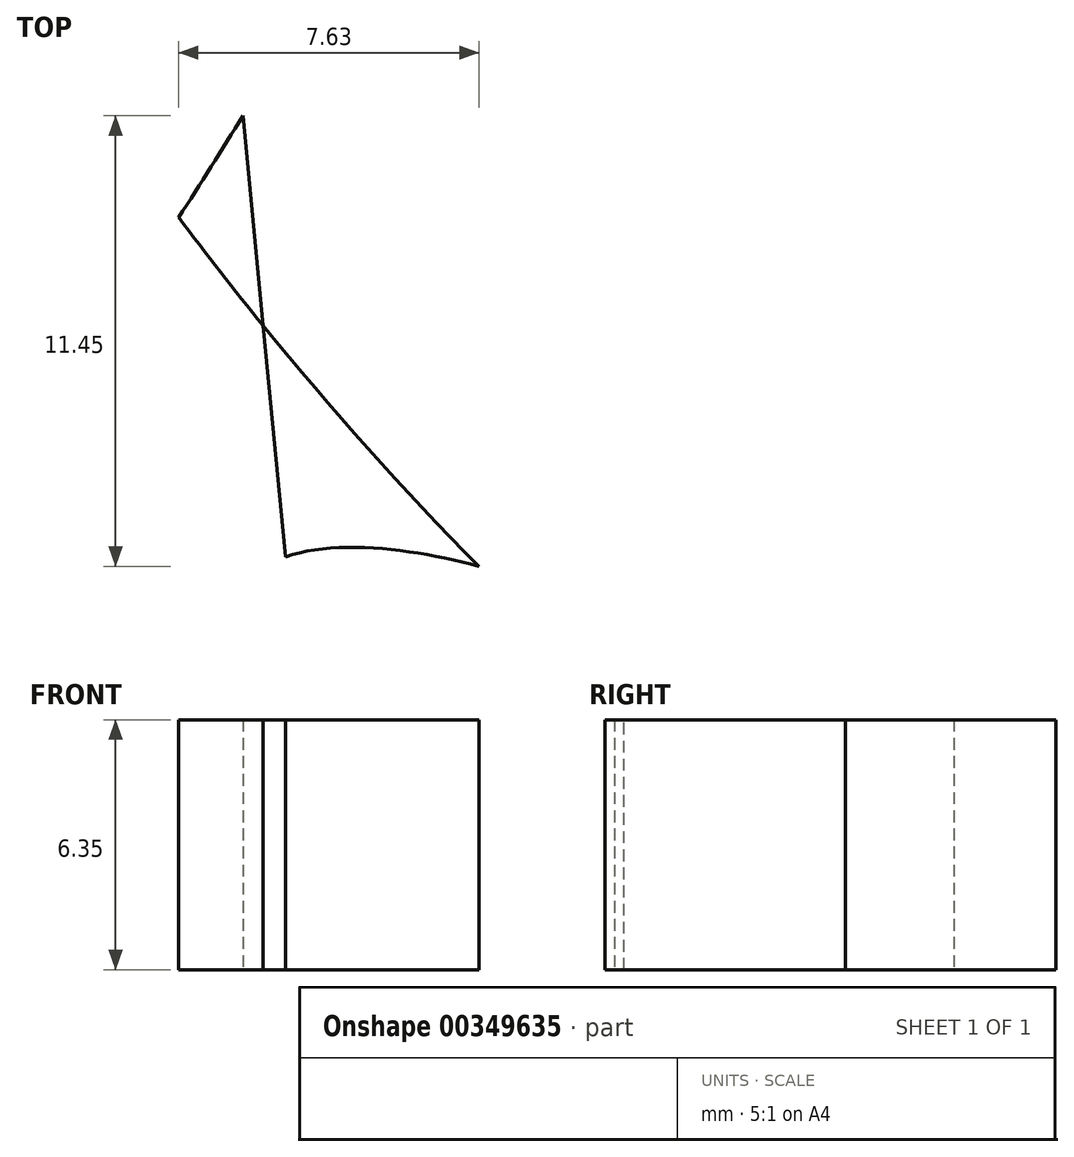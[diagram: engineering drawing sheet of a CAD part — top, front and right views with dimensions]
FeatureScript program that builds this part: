
annotation { "Feature Type Name" : "Feature", "Feature Type Description" : "" }
export const myFeature = defineFeature(function(context is Context, id is Id, definition is map)
    precondition{}
    {
        {
            var Q0;
            Q0=qCreatedBy(makeId("Top.planeOp"),FACE);
            var sketch = newSketch(context, id + "F0", { "sketchPlane" : qUnion([Q0])});
            skFitSpline(sketch, "E0", {"points": [v(-89.2, -72.37) * mm, v(-80.96, -69.32) * mm, v(-70.58, -66.57) * mm, v(-58.06, -63.52) * mm, v(-42.18, -61.08) * mm, v(-30.58, -59.24) * mm, v(-14.4, -58.33) * mm, v(2.7, -58.02) * mm, v(24.38, -58.02) * mm, v(45.14, -58.02) * mm, v(71.09, -58.02) * mm, v(96.43, -58.02) * mm, v(117.7, -59.07) * mm, v(146.1, -60.85) * mm, v(171.42, -62.58) * mm, v(182.87, -63.62) * mm, v(192.92, -64.66) * mm, v(205.06, -67.78) * mm, v(216.16, -72.64) * mm, v(220.67, -74.37) * mm, v(223.44, -78.54) * mm, v(225.87, -86.51) * mm, v(223.1, -93.8) * mm, v(217.2, -101.77) * mm, v(210.26, -105.24) * mm, v(204.02, -105.59) * mm, v(197.78, -102.81) * mm, v(185.99, -97.26) * mm, v(172.11, -92.4) * mm, v(159.28, -89.63) * mm, v(141.94, -86.51) * mm, v(125.64, -85.82) * mm, v(113.85, -86.17) * mm, v(104.49, -86.51) * mm, v(97.2, -88.94) * mm, v(93.04, -92.4) * mm, v(90.61, -95.88) * mm, v(89.23, -99) * mm, v(87.84, -100.73) * mm, v(85.41, -99.34) * mm, v(83.92, -93.7) * mm, v(81.94, -88.7) * mm, v(78.82, -86.86) * mm, v(73.53, -86.51) * mm, v(71.54, -88.6) * mm, v(70.85, -90.67) * mm, v(69.11, -92.06) * mm, v(62.87, -91.02) * mm, v(58.01, -89.98) * mm, v(49, -89.98) * mm, v(36.86, -91.02) * mm, v(24.72, -93.1) * mm, v(16.4, -94.84) * mm, v(6, -96.57) * mm, v(-5.1, -99.34) * mm, v(-19.67, -100.73) * mm, v(-29.38, -101.08) * mm, v(-37.36, -100.73) * mm, v(-44.3, -100.04) * mm, v(-54.7, -97.96) * mm, v(-61.98, -95.18) * mm, v(-71, -89.98) * mm, v(-75.86, -85.82) * mm, v(-89.2, -72.37) * mm]});
            skPoint(sketch, "E1.1.internal.orphan", {"position": v(73.53, -78.42) * mm});
            skPoint(sketch, "E2.1.internal.orphan", {"position": v(72.1, -82.53) * mm});
            skPoint(sketch, "E3.1.internal.orphan", {"position": v(73.53, -82.53) * mm});
            skLineSegment(sketch, "E4", {"start": v(73.53, -86.51) * mm, "end": v(71.83, -68.93) * mm});
            skLineSegment(sketch, "E5", {"start": v(68.17, -65.48) * mm, "end": v(-44.06, -61.37) * mm});
            skPoint(sketch, "E6.visualSharp", {"position": v(71.5, -65.6) * mm});
            skArc(sketch, "E6.filletArc", {"start": v(71.83, -68.93) * mm, "mid": v(70.65, -66.52) * mm, "end": v(68.17, -65.48) * mm});
            skCircle(sketch, "E7", {"center": v(209.21, -94.51) * mm, "radius": 4.76 * mm});
            skPoint(sketch, "E7.first.point", {"position": v(209.05, -99.27) * mm});
            skPoint(sketch, "E7.second.point", {"position": v(209.18, -89.75) * mm});
            skPoint(sketch, "E7.third.point", {"position": v(213.88, -93.56) * mm});
            skCircle(sketch, "E8", {"center": v(191.7, -78.8) * mm, "radius": 3.18 * mm});
            skPoint(sketch, "E8.first.point", {"position": v(191.75, -81.97) * mm});
            skPoint(sketch, "E8.second.point", {"position": v(191.63, -75.62) * mm});
            skPoint(sketch, "E8.third.point", {"position": v(194.8, -78.19) * mm});
            skCircle(sketch, "E9", {"center": v(123.5, -71.58) * mm, "radius": 3.18 * mm});
            skPoint(sketch, "E9.first.point", {"position": v(120.34, -71.87) * mm});
            skPoint(sketch, "E9.second.point", {"position": v(126.65, -71.2) * mm});
            skPoint(sketch, "E9.third.point", {"position": v(124.1, -74.7) * mm});
            skLineSegment(sketch, "E10", {"start": v(142.3, -60.6) * mm, "end": v(154.42, -61.38) * mm});
            skPoint(sketch, "E11.start.orphan", {"position": v(154.42, -70.9) * mm});
            skArc(sketch, "E12", {"start": v(172.79, -52.87) * mm, "mid": v(160.07, -46.61) * mm, "end": v(146.76, -51.46) * mm});
            skArc(sketch, "E13", {"start": v(220.67, -74.37) * mm, "mid": v(193.32, -64.98) * mm, "end": v(164.55, -62.06) * mm});
            skArc(sketch, "E14", {"start": v(220.67, -74.37) * mm, "mid": v(220.11, -81.8) * mm, "end": v(225.87, -86.51) * mm});
            skArc(sketch, "E15", {"start": v(8.92, 3.57) * mm, "mid": v(-27.84, 5.96) * mm, "end": v(-64.6, 8.29) * mm});
            skArc(sketch, "E16", {"start": v(54.16, -6.04) * mm, "mid": v(32.02, 1.01) * mm, "end": v(8.92, 3.57) * mm});
            skArc(sketch, "E17", {"start": v(225.22, -17.28) * mm, "mid": v(145.31, 73.87) * mm, "end": v(54.16, -6.04) * mm});
            skArc(sketch, "E18", {"start": v(54.16, -35.45) * mm, "mid": v(148.77, -111.9) * mm, "end": v(225.22, -17.28) * mm});
            skArc(sketch, "E19", {"start": v(202.98, -36.51) * mm, "mid": v(129.1, 38.43) * mm, "end": v(54.16, -35.45) * mm});
            skArc(sketch, "E20", {"start": v(202.98, -36.51) * mm, "mid": v(191.08, -30.63) * mm, "end": v(178.66, -25.96) * mm});
            skArc(sketch, "E21", {"start": v(178.66, -25.96) * mm, "mid": v(162.48, -21.52) * mm, "end": v(145.86, -19.17) * mm});
            skArc(sketch, "E22", {"start": v(145.86, -19.17) * mm, "mid": v(128.87, -16.97) * mm, "end": v(111.74, -17.28) * mm});
            skArc(sketch, "E23", {"start": v(111.74, -17.28) * mm, "mid": v(105.33, -17.9) * mm, "end": v(99.11, -19.55) * mm});
            skArc(sketch, "E24", {"start": v(99.11, -19.55) * mm, "mid": v(92.44, -23.97) * mm, "end": v(88.37, -30.86) * mm});
            skArc(sketch, "E25", {"start": v(84.03, -27.28) * mm, "mid": v(85.3, -30.16) * mm, "end": v(88.37, -30.86) * mm});
            skArc(sketch, "E26", {"start": v(-71.95, 0.18) * mm, "mid": v(-11.54, -113.43) * mm, "end": v(84.03, -27.28) * mm});
            skArc(sketch, "E27", {"start": v(-64.6, 8.29) * mm, "mid": v(-68.86, 4.76) * mm, "end": v(-71.95, 0.18) * mm});
            skSolve(sketch);
        }
        {
            var Q0;
            {var subQ0=sQuery(id+"F0.wireOp",EDGE,"E4");Q0=makeQuery(id+"F0.imprint","IMPRINT",FACE,{"disambiguationData":[TD([[makeQuery(id+"F0.imprint","IMPRINT",EDGE,{"derivedFrom":subQ0}),-1.0]])]});}
            extrude(context, id + "F1", {"entities" : qUnion([Q0]), "depth" : 6.35 * mm});
        }
        {
            var Q0;
            {var subQ0=sQuery(id+"F0.wireOp",EDGE,"E4");Q0=makeQuery(id+"F0.imprint","IMPRINT",FACE,{"disambiguationData":[TD([[makeQuery(id+"F0.imprint","IMPRINT",EDGE,{"derivedFrom":subQ0}),1.0]])]});}
            extrude(context, id + "F2", {"entities" : qUnion([Q0]), "depth" : 6.35 * mm});
        }
    });
